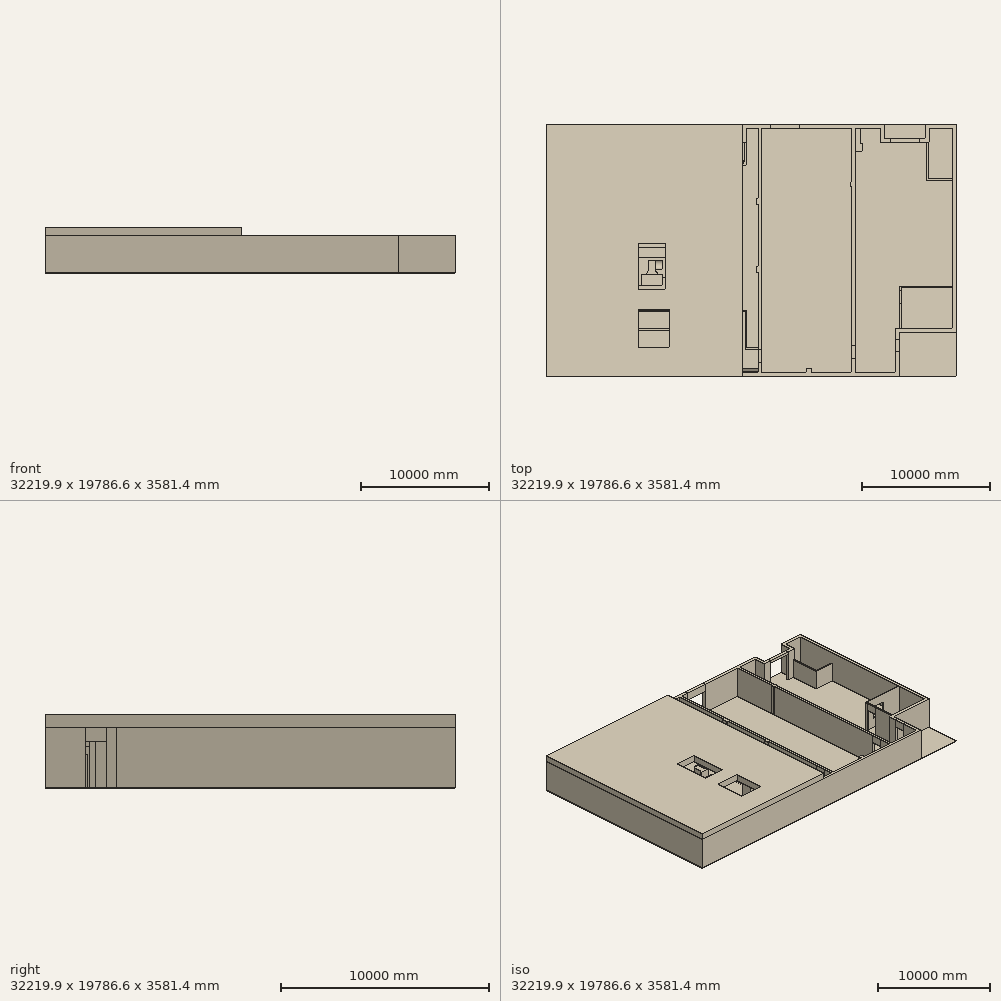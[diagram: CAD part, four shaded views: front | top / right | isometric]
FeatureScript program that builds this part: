
annotation { "Feature Type Name" : "Feature", "Feature Type Description" : "" }
export const myFeature = defineFeature(function(context is Context, id is Id, definition is map)
    precondition{}
    {
        {
            var Q0;
            Q0=qCreatedBy(makeId("Top.planeOp"),FACE);
            var sketch = newSketch(context, id + "F0", { "sketchPlane" : qUnion([Q0])});
            skLineSegment(sketch, "E0.bottom", {"start": v(-292.1, 292.1) * mm, "end": v(31927.8, 292.1) * mm});
            skLineSegment(sketch, "E0.top", {"start": v(-292.1, -19494.5) * mm, "end": v(31927.8, -19494.5) * mm});
            skLineSegment(sketch, "E0.left", {"start": v(-292.1, 292.1) * mm, "end": v(-292.1, -19494.5) * mm});
            skLineSegment(sketch, "E0.right", {"start": v(31927.8, 292.1) * mm, "end": v(31927.8, -19494.5) * mm});
            skSolve(sketch);
        }
        {
            var Q0;
            Q0 = qSketchRegion(id + "F0", true);
            extrude(context, id + "F1", {"entities" : qUnion([Q0]), "oppositeDirection" : true, "depth" : 50.8 * mm});
        }
        {
            var Q0;
            Q0=qCreatedBy(makeId("Top.planeOp"),FACE);
            var sketch = newSketch(context, id + "F2", { "sketchPlane" : qUnion([Q0])});
            skLineSegment(sketch, "E1.bottom", {"start": v(0, 0) * mm, "end": v(3479.8, 0) * mm});
            skLineSegment(sketch, "E1.top", {"start": v(0, -18897.6) * mm, "end": v(6451.6, -18897.6) * mm, "construction": true});
            skLineSegment(sketch, "E1.left", {"start": v(0, 0) * mm, "end": v(0, -18897.6) * mm});
            skLineSegment(sketch, "E1.right", {"start": v(16332.2, 0) * mm, "end": v(16332.2, -5537.2) * mm});
            skLineSegment(sketch, "E2.top", {"start": v(0, -19202.4) * mm, "end": v(6451.6, -19202.4) * mm});
            skLineSegment(sketch, "E2.left", {"start": v(0, -18897.6) * mm, "end": v(0, -19202.4) * mm});
            skLineSegment(sketch, "E2.right", {"start": v(16332.2, -18897.6) * mm, "end": v(16332.2, -19202.4) * mm});
            skLineSegment(sketch, "E3", {"start": v(0, -4508.5) * mm, "end": v(3479.8, -4508.5) * mm, "construction": true});
            skLineSegment(sketch, "E4", {"start": v(3479.8, -4508.5) * mm, "end": v(3479.8, -4457.7) * mm, "construction": true});
            skLineSegment(sketch, "E5", {"start": v(3479.8, -4457.7) * mm, "end": v(3594.1, -4457.7) * mm, "construction": true});
            skLineSegment(sketch, "E6", {"start": v(3594.1, -4457.7) * mm, "end": v(3594.1, -4622.8) * mm, "construction": true});
            skLineSegment(sketch, "E7", {"start": v(3594.1, -4622.8) * mm, "end": v(0, -4622.8) * mm, "construction": true});
            skLineSegment(sketch, "E8", {"start": v(3479.8, 0) * mm, "end": v(3479.8, -1117.6) * mm});
            skLineSegment(sketch, "E9", {"start": v(3479.8, -1117.6) * mm, "end": v(4267.2, -1117.6) * mm});
            skLineSegment(sketch, "E10", {"start": v(4267.2, -1117.6) * mm, "end": v(4267.2, -825.5) * mm});
            skLineSegment(sketch, "E11", {"start": v(4267.2, -825.5) * mm, "end": v(3771.9, -825.5) * mm});
            skLineSegment(sketch, "E12", {"start": v(3771.9, -825.5) * mm, "end": v(3771.9, 0) * mm});
            skLineSegment(sketch, "E13", {"start": v(5295.9, -825.5) * mm, "end": v(5295.9, -1117.6) * mm});
            skLineSegment(sketch, "E14", {"start": v(5295.9, -1117.6) * mm, "end": v(6096, -1117.6) * mm});
            skLineSegment(sketch, "E15", {"start": v(6096, -1117.6) * mm, "end": v(6096, 0) * mm});
            skLineSegment(sketch, "E16", {"start": v(5295.9, -825.5) * mm, "end": v(5803.9, -825.5) * mm});
            skLineSegment(sketch, "E17", {"start": v(5803.9, -825.5) * mm, "end": v(5803.9, 0) * mm});
            skLineSegment(sketch, "E18", {"start": v(3479.8, -1117.6) * mm, "end": v(3479.8, -3543.3) * mm, "construction": true});
            skLineSegment(sketch, "E19", {"start": v(3479.8, -3543.3) * mm, "end": v(3594.1, -3543.3) * mm, "construction": true});
            skLineSegment(sketch, "E20", {"start": v(3594.1, -3543.3) * mm, "end": v(3594.1, -1117.6) * mm, "construction": true});
            skLineSegment(sketch, "E21", {"start": v(11582.4, 0) * mm, "end": v(11582.4, -1117.6) * mm});
            skLineSegment(sketch, "E22", {"start": v(11582.4, -1117.6) * mm, "end": v(12382.5, -1117.6) * mm});
            skLineSegment(sketch, "E23", {"start": v(12382.5, -1117.6) * mm, "end": v(12382.5, -825.5) * mm});
            skLineSegment(sketch, "E24", {"start": v(12382.5, -825.5) * mm, "end": v(11874.5, -825.5) * mm});
            skLineSegment(sketch, "E25", {"start": v(11874.5, -825.5) * mm, "end": v(11874.5, 0) * mm});
            skLineSegment(sketch, "E26", {"start": v(15113, 0) * mm, "end": v(15113, -825.5) * mm});
            skLineSegment(sketch, "E27", {"start": v(15113, -825.5) * mm, "end": v(14605, -825.5) * mm});
            skLineSegment(sketch, "E28", {"start": v(14605, -825.5) * mm, "end": v(14605, -1117.6) * mm});
            skLineSegment(sketch, "E29", {"start": v(14605, -1117.6) * mm, "end": v(15405.1, -1117.6) * mm});
            skLineSegment(sketch, "E30", {"start": v(15405.1, -1117.6) * mm, "end": v(15405.1, 0) * mm});
            skLineSegment(sketch, "E31", {"start": v(3771.9, 0) * mm, "end": v(3771.9, 292.1) * mm});
            skLineSegment(sketch, "E32", {"start": v(3771.9, 292.1) * mm, "end": v(-292.1, 292.1) * mm});
            skLineSegment(sketch, "E33", {"start": v(-292.1, 292.1) * mm, "end": v(-292.1, -19494.5) * mm});
            skLineSegment(sketch, "E34", {"start": v(-292.1, -19494.5) * mm, "end": v(16624.3, -19494.5) * mm});
            skLineSegment(sketch, "E35", {"start": v(16624.3, -19202.4) * mm, "end": v(16624.3, -18376.9) * mm});
            skLineSegment(sketch, "E36", {"start": v(16624.3, 292.1) * mm, "end": v(15113, 292.1) * mm});
            skLineSegment(sketch, "E37", {"start": v(15113, 292.1) * mm, "end": v(15113, 0) * mm});
            skLineSegment(sketch, "E38", {"start": v(5803.9, 0) * mm, "end": v(5803.9, 292.1) * mm});
            skLineSegment(sketch, "E39", {"start": v(5803.9, 292.1) * mm, "end": v(11874.5, 292.1) * mm});
            skLineSegment(sketch, "E40", {"start": v(11874.5, 292.1) * mm, "end": v(11874.5, 0) * mm});
            skLineSegment(sketch, "E41.trimOffspring", {"start": v(6096, 0) * mm, "end": v(11582.4, 0) * mm});
            skLineSegment(sketch, "E42.trimOffspring", {"start": v(15405.1, 0) * mm, "end": v(16332.2, 0) * mm});
            skLineSegment(sketch, "E43", {"start": v(16332.2, -18376.9) * mm, "end": v(16624.3, -18376.9) * mm});
            skLineSegment(sketch, "E44", {"start": v(16624.3, -17348.2) * mm, "end": v(16332.2, -17348.2) * mm});
            skLineSegment(sketch, "E45.trimOffspring", {"start": v(16332.2, -18376.9) * mm, "end": v(16332.2, -18897.6) * mm});
            skLineSegment(sketch, "E46.trimOffspring", {"start": v(16624.3, -17348.2) * mm, "end": v(16624.3, 0) * mm});
            skLineSegment(sketch, "E47", {"start": v(16332.2, -5537.2) * mm, "end": v(16230.6, -5537.2) * mm});
            skLineSegment(sketch, "E48", {"start": v(16230.6, -5537.2) * mm, "end": v(16230.6, -6007.1) * mm});
            skLineSegment(sketch, "E49", {"start": v(16230.6, -6007.1) * mm, "end": v(16332.2, -6007.1) * mm});
            skLineSegment(sketch, "E50", {"start": v(16332.2, -10833.1) * mm, "end": v(16230.6, -10833.1) * mm});
            skLineSegment(sketch, "E51", {"start": v(16230.6, -10833.1) * mm, "end": v(16230.6, -11303) * mm});
            skLineSegment(sketch, "E52", {"start": v(16230.6, -11303) * mm, "end": v(16332.2, -11303) * mm});
            skLineSegment(sketch, "E53.trimOffspring", {"start": v(16332.2, -11303) * mm, "end": v(16332.2, -17348.2) * mm});
            skLineSegment(sketch, "E54.trimOffspring", {"start": v(16332.2, -6007.1) * mm, "end": v(16332.2, -10833.1) * mm});
            skLineSegment(sketch, "E55", {"start": v(6451.6, -19202.4) * mm, "end": v(6451.6, -18897.6) * mm});
            skLineSegment(sketch, "E56", {"start": v(6845.3, -19202.4) * mm, "end": v(6845.3, -18897.6) * mm});
            skLineSegment(sketch, "E57", {"start": v(9982.2, -19151.6) * mm, "end": v(9982.2, -18897.6) * mm});
            skLineSegment(sketch, "E58", {"start": v(10337.8, -19151.6) * mm, "end": v(10337.8, -18897.6) * mm});
            skLineSegment(sketch, "E59", {"start": v(13309.6, -19202.4) * mm, "end": v(13309.6, -18897.6) * mm});
            skLineSegment(sketch, "E60", {"start": v(13700.76, -19202.4) * mm, "end": v(13700.76, -18897.6) * mm});
            skLineSegment(sketch, "E61.trimOffspring", {"start": v(6845.3, -18897.6) * mm, "end": v(9982.2, -18897.6) * mm, "construction": true});
            skLineSegment(sketch, "E62.trimOffspring", {"start": v(6845.3, -19202.4) * mm, "end": v(9982.2, -19202.4) * mm});
            skLineSegment(sketch, "E63.trimOffspring", {"start": v(10337.8, -18897.6) * mm, "end": v(13309.6, -18897.6) * mm, "construction": true});
            skLineSegment(sketch, "E64.trimOffspring", {"start": v(10337.8, -19202.4) * mm, "end": v(13309.6, -19202.4) * mm});
            skLineSegment(sketch, "E65.trimOffspring", {"start": v(13700.76, -18897.6) * mm, "end": v(16332.2, -18897.6) * mm, "construction": true});
            skLineSegment(sketch, "E66.trimOffspring", {"start": v(13700.76, -19202.4) * mm, "end": v(16332.2, -19202.4) * mm});
            skLineSegment(sketch, "E67", {"start": v(6451.6, -18897.6) * mm, "end": v(6845.3, -18897.6) * mm});
            skLineSegment(sketch, "E68", {"start": v(9982.2, -18897.6) * mm, "end": v(10337.8, -18897.6) * mm});
            skLineSegment(sketch, "E69", {"start": v(13309.6, -18897.6) * mm, "end": v(13700.76, -18897.6) * mm});
            skLineSegment(sketch, "E70", {"start": v(9982.2, -19151.6) * mm, "end": v(10337.8, -19151.6) * mm});
            skLineSegment(sketch, "E71", {"start": v(10337.8, -19202.4) * mm, "end": v(9982.2, -19202.4) * mm});
            skLineSegment(sketch, "E72.bottom", {"start": v(9944.1, -4292.6) * mm, "end": v(10261.6, -4292.6) * mm});
            skLineSegment(sketch, "E72.top", {"start": v(9944.1, -4610.1) * mm, "end": v(10261.6, -4610.1) * mm});
            skLineSegment(sketch, "E72.left", {"start": v(9944.1, -4292.6) * mm, "end": v(9944.1, -4610.1) * mm});
            skLineSegment(sketch, "E72.right", {"start": v(10261.6, -4292.6) * mm, "end": v(10261.6, -4610.1) * mm});
            skLineSegment(sketch, "E73", {"start": v(16332.2, -18897.6) * mm, "end": v(34945.72, -18897.6) * mm, "construction": true});
            skLineSegment(sketch, "E74", {"start": v(16624.3, -19202.4) * mm, "end": v(20129.5, -19202.4) * mm});
            skLineSegment(sketch, "E75", {"start": v(16624.3, -19494.5) * mm, "end": v(27432, -19494.5) * mm});
            skLineSegment(sketch, "E76", {"start": v(27432, -19494.5) * mm, "end": v(27432, -17576.8) * mm});
            skLineSegment(sketch, "E77", {"start": v(27432, -16052.8) * mm, "end": v(31927.8, -16052.8) * mm});
            skLineSegment(sketch, "E78", {"start": v(31927.8, -16052.8) * mm, "end": v(31927.8, 292.1) * mm});
            skLineSegment(sketch, "E79", {"start": v(16624.3, 0) * mm, "end": v(17335.5, 0) * mm});
            skLineSegment(sketch, "E80", {"start": v(25946.1, 0) * mm, "end": v(25946.1, -1117.6) * mm});
            skLineSegment(sketch, "E81", {"start": v(25946.1, -1117.6) * mm, "end": v(26746.2, -1117.6) * mm});
            skLineSegment(sketch, "E82", {"start": v(26746.2, -1117.6) * mm, "end": v(26746.2, -825.5) * mm});
            skLineSegment(sketch, "E83", {"start": v(26746.2, -825.5) * mm, "end": v(26238.2, -825.5) * mm});
            skLineSegment(sketch, "E84", {"start": v(26238.2, -825.5) * mm, "end": v(26238.2, 292.1) * mm});
            skLineSegment(sketch, "E85", {"start": v(26238.2, 292.1) * mm, "end": v(19558, 292.1) * mm});
            skLineSegment(sketch, "E86", {"start": v(17335.5, 292.1) * mm, "end": v(17335.5, 0) * mm});
            skLineSegment(sketch, "E87", {"start": v(19558, 0) * mm, "end": v(19558, 292.1) * mm});
            skLineSegment(sketch, "E88.trimOffspring", {"start": v(17335.5, 292.1) * mm, "end": v(16624.3, 292.1) * mm});
            skLineSegment(sketch, "E89.trimOffspring", {"start": v(19558, 0) * mm, "end": v(23672.8, 0) * mm});
            skLineSegment(sketch, "E90", {"start": v(23672.8, 0) * mm, "end": v(23672.8, -4292.6) * mm});
            skLineSegment(sketch, "E91", {"start": v(23964.9, 0) * mm, "end": v(23964.9, -4292.6) * mm});
            skLineSegment(sketch, "E92", {"start": v(23964.9, -19202.4) * mm, "end": v(27139.9, -19202.4) * mm});
            skLineSegment(sketch, "E93", {"start": v(27139.9, -19202.4) * mm, "end": v(27139.9, -17576.8) * mm});
            skLineSegment(sketch, "E94", {"start": v(27139.9, -15760.7) * mm, "end": v(31635.7, -15760.7) * mm});
            skLineSegment(sketch, "E95", {"start": v(31635.7, -15760.7) * mm, "end": v(31635.7, 0) * mm});
            skLineSegment(sketch, "E96", {"start": v(31635.7, 0) * mm, "end": v(29781.5, 0) * mm});
            skLineSegment(sketch, "E97", {"start": v(29781.5, 0) * mm, "end": v(29781.5, -1117.6) * mm});
            skLineSegment(sketch, "E98", {"start": v(29781.5, -1117.6) * mm, "end": v(28981.4, -1117.6) * mm});
            skLineSegment(sketch, "E99", {"start": v(28981.4, -1117.6) * mm, "end": v(28981.4, -825.5) * mm});
            skLineSegment(sketch, "E100", {"start": v(28981.4, -825.5) * mm, "end": v(29489.4, -825.5) * mm});
            skLineSegment(sketch, "E101", {"start": v(29489.4, -825.5) * mm, "end": v(29489.4, 292.1) * mm});
            skLineSegment(sketch, "E102", {"start": v(29489.4, 292.1) * mm, "end": v(31927.8, 292.1) * mm});
            skLineSegment(sketch, "E103.trimOffspring", {"start": v(23964.9, 0) * mm, "end": v(25946.1, 0) * mm});
            skLineSegment(sketch, "E104", {"start": v(27139.9, -16560.8) * mm, "end": v(27432, -16560.8) * mm});
            skLineSegment(sketch, "E105", {"start": v(27139.9, -17576.8) * mm, "end": v(27432, -17576.8) * mm});
            skLineSegment(sketch, "E106.trimOffspring", {"start": v(27432, -16560.8) * mm, "end": v(27432, -16052.8) * mm});
            skLineSegment(sketch, "E107.trimOffspring", {"start": v(27139.9, -16560.8) * mm, "end": v(27139.9, -15760.7) * mm});
            skLineSegment(sketch, "E108", {"start": v(20129.5, -19202.4) * mm, "end": v(20129.5, -18897.6) * mm});
            skLineSegment(sketch, "E109", {"start": v(20129.5, -18897.6) * mm, "end": v(20535.9, -18897.6) * mm});
            skLineSegment(sketch, "E110", {"start": v(20535.9, -18897.6) * mm, "end": v(20535.9, -19202.4) * mm});
            skLineSegment(sketch, "E111.trimOffspring", {"start": v(20535.9, -19202.4) * mm, "end": v(23672.8, -19202.4) * mm});
            skLineSegment(sketch, "E112", {"start": v(23672.8, -17068.8) * mm, "end": v(23964.9, -17068.8) * mm});
            skLineSegment(sketch, "E113", {"start": v(23964.9, -18084.8) * mm, "end": v(23672.8, -18084.8) * mm});
            skLineSegment(sketch, "E114.trimOffspring", {"start": v(23964.9, -18084.8) * mm, "end": v(23964.9, -19202.4) * mm});
            skLineSegment(sketch, "E115.trimOffspring", {"start": v(23672.8, -18084.8) * mm, "end": v(23672.8, -19202.4) * mm});
            skLineSegment(sketch, "E116", {"start": v(23672.8, -4292.6) * mm, "end": v(23634.7, -4292.6) * mm});
            skLineSegment(sketch, "E117", {"start": v(23634.7, -4292.6) * mm, "end": v(23634.7, -4610.1) * mm});
            skLineSegment(sketch, "E118", {"start": v(23634.7, -4610.1) * mm, "end": v(23672.8, -4610.1) * mm});
            skLineSegment(sketch, "E119", {"start": v(23964.9, -4292.6) * mm, "end": v(24003, -4292.6) * mm});
            skLineSegment(sketch, "E120", {"start": v(24003, -4292.6) * mm, "end": v(24003, -4610.1) * mm});
            skLineSegment(sketch, "E121", {"start": v(24003, -4610.1) * mm, "end": v(23964.9, -4610.1) * mm});
            skLineSegment(sketch, "E122.trimOffspring", {"start": v(23672.8, -4610.1) * mm, "end": v(23672.8, -17068.8) * mm});
            skLineSegment(sketch, "E123.trimOffspring", {"start": v(23964.9, -4610.1) * mm, "end": v(23964.9, -17068.8) * mm});
            skSolve(sketch);
        }
        {
            var Q0;
            Q0 = qSketchRegion(id + "F2", true);
            extrude(context, id + "F3", {"entities" : qUnion([Q0]), "depth" : 2921 * mm});
        }
        {
            var Q0;
            Q0=makeQuery(id+"F3.opExtrude","SWEPT_FACE",FACE,{"disambiguationData":[OSD([sQuery(id+"F2.wireOp",EDGE,"E2.right"),sQuery(id+"F2.wireOp",EDGE,"E45.trimOffspring")])]});
            var sketch = newSketch(context, id + "F4", { "sketchPlane" : qUnion([Q0])});
            skLineSegment(sketch, "E124", {"start": v(19202.4, 0) * mm, "end": v(18897.6, 0) * mm});
            skLineSegment(sketch, "E125", {"start": v(18897.6, 0) * mm, "end": v(18897.6, 203.2) * mm});
            skLineSegment(sketch, "E126", {"start": v(18897.6, 203.2) * mm, "end": v(19100.8, 457.2) * mm});
            skLineSegment(sketch, "E127", {"start": v(19202.4, 457.2) * mm, "end": v(19202.4, 0) * mm});
            skLineSegment(sketch, "E128", {"start": v(19202.4, 457.2) * mm, "end": v(19100.8, 457.2) * mm});
            skSolve(sketch);
        }
        {
            var Q0;
            Q0 = qSketchRegion(id + "F4", true);
            var Q1;
            Q1=makeQuery(id+"F3.opExtrude","SWEPT_FACE",FACE,{"disambiguationData":[OSD([sQuery(id+"F2.wireOp",EDGE,"E1.left"),sQuery(id+"F2.wireOp",EDGE,"E2.left")])]});
            extrude(context, id + "F5", {"entities" : qUnion([Q0]), "endBound" : BoundingType.UP_TO_SURFACE, "endBoundEntityFace" : qUnion([Q1]), "depth" : 25.4 * mm});
        }
        {
            var Q0;
            Q0=makeQuery(id+"F1.opExtrude","CAP_FACE",FACE,{"disambiguationData":[OSD([sQuery(id+"F0.wireOp",EDGE,"E0.bottom"),sQuery(id+"F0.wireOp",EDGE,"E0.top"),sQuery(id+"F0.wireOp",EDGE,"E0.left"),sQuery(id+"F0.wireOp",EDGE,"E0.right")])],"isStart":true});
            var sketch = newSketch(context, id + "F6", { "sketchPlane" : qUnion([Q0])});
            skLineSegment(sketch, "E129", {"start": v(3479.8, -1117.6) * mm, "end": v(3479.8, -3543.3) * mm});
            skLineSegment(sketch, "E130", {"start": v(3479.8, -3543.3) * mm, "end": v(3594.1, -3543.3) * mm});
            skLineSegment(sketch, "E131", {"start": v(3594.1, -3543.3) * mm, "end": v(3594.1, -1117.6) * mm});
            skLineSegment(sketch, "E132", {"start": v(3594.1, -1117.6) * mm, "end": v(3479.8, -1117.6) * mm});
            skLineSegment(sketch, "E133", {"start": v(0, -4508.5) * mm, "end": v(3479.8, -4508.5) * mm});
            skLineSegment(sketch, "E134", {"start": v(3479.8, -4508.5) * mm, "end": v(3479.8, -4457.7) * mm});
            skLineSegment(sketch, "E135", {"start": v(3479.8, -4457.7) * mm, "end": v(3594.1, -4457.7) * mm});
            skLineSegment(sketch, "E136", {"start": v(3594.1, -4457.7) * mm, "end": v(3594.1, -4622.8) * mm});
            skLineSegment(sketch, "E137", {"start": v(3594.1, -4622.8) * mm, "end": v(0, -4622.8) * mm});
            skLineSegment(sketch, "E138", {"start": v(0, -4622.8) * mm, "end": v(0, -4508.5) * mm});
            skSolve(sketch);
        }
        {
            var Q0;
            Q0 = qSketchRegion(id + "F6", true);
            extrude(context, id + "F7", {"entities" : qUnion([Q0]), "depth" : 2921 * mm});
        }
        {
            var Q0;
            Q0=makeQuery(id+"F3.opExtrude","CAP_FACE",FACE,{"disambiguationData":[OSD([sQuery(id+"F2.wireOp",EDGE,"E13"),sQuery(id+"F2.wireOp",EDGE,"E14"),sQuery(id+"F2.wireOp",EDGE,"E15"),sQuery(id+"F2.wireOp",EDGE,"E16"),sQuery(id+"F2.wireOp",EDGE,"E17"),sQuery(id+"F2.wireOp",EDGE,"E21"),sQuery(id+"F2.wireOp",EDGE,"E22"),sQuery(id+"F2.wireOp",EDGE,"E23"),sQuery(id+"F2.wireOp",EDGE,"E24"),sQuery(id+"F2.wireOp",EDGE,"E25"),sQuery(id+"F2.wireOp",EDGE,"E38"),sQuery(id+"F2.wireOp",EDGE,"E39"),sQuery(id+"F2.wireOp",EDGE,"E40"),sQuery(id+"F2.wireOp",EDGE,"E41.trimOffspring")])],"isStart":false});
            var sketch = newSketch(context, id + "F8", { "sketchPlane" : qUnion([Q0])});
            skLineSegment(sketch, "E139.bottom", {"start": v(4267.2, -825.5) * mm, "end": v(5295.9, -825.5) * mm});
            skLineSegment(sketch, "E139.top", {"start": v(4267.2, -1117.6) * mm, "end": v(5295.9, -1117.6) * mm});
            skLineSegment(sketch, "E139.left", {"start": v(4267.2, -825.5) * mm, "end": v(4267.2, -1117.6) * mm});
            skLineSegment(sketch, "E139.right", {"start": v(5295.9, -825.5) * mm, "end": v(5295.9, -1117.6) * mm});
            skLineSegment(sketch, "E140.bottom", {"start": v(16624.3, -17348.2) * mm, "end": v(16332.2, -17348.2) * mm});
            skLineSegment(sketch, "E140.top", {"start": v(16624.3, -18376.9) * mm, "end": v(16332.2, -18376.9) * mm});
            skLineSegment(sketch, "E140.left", {"start": v(16624.3, -17348.2) * mm, "end": v(16624.3, -18376.9) * mm});
            skLineSegment(sketch, "E140.right", {"start": v(16332.2, -17348.2) * mm, "end": v(16332.2, -18376.9) * mm});
            skLineSegment(sketch, "E141.bottom", {"start": v(23672.8, -17068.8) * mm, "end": v(23964.9, -17068.8) * mm});
            skLineSegment(sketch, "E141.top", {"start": v(23672.8, -18084.8) * mm, "end": v(23964.9, -18084.8) * mm});
            skLineSegment(sketch, "E141.left", {"start": v(23672.8, -17068.8) * mm, "end": v(23672.8, -18084.8) * mm});
            skLineSegment(sketch, "E141.right", {"start": v(23964.9, -17068.8) * mm, "end": v(23964.9, -18084.8) * mm});
            skLineSegment(sketch, "E142.bottom", {"start": v(27139.9, -16560.8) * mm, "end": v(27432, -16560.8) * mm});
            skLineSegment(sketch, "E142.top", {"start": v(27139.9, -17576.8) * mm, "end": v(27432, -17576.8) * mm});
            skLineSegment(sketch, "E142.left", {"start": v(27139.9, -16560.8) * mm, "end": v(27139.9, -17576.8) * mm});
            skLineSegment(sketch, "E142.right", {"start": v(27432, -16560.8) * mm, "end": v(27432, -17576.8) * mm});
            skLineSegment(sketch, "E143.bottom", {"start": v(17335.5, 292.1) * mm, "end": v(19558, 292.1) * mm});
            skLineSegment(sketch, "E143.top", {"start": v(17335.5, 0) * mm, "end": v(19558, 0) * mm});
            skLineSegment(sketch, "E143.left", {"start": v(17335.5, 292.1) * mm, "end": v(17335.5, 0) * mm});
            skLineSegment(sketch, "E143.right", {"start": v(19558, 292.1) * mm, "end": v(19558, 0) * mm});
            skSolve(sketch);
        }
        {
            var Q0;
            Q0 = qSketchRegion(id + "F8", true);
            extrude(context, id + "F9", {"entities" : qUnion([Q0]), "oppositeDirection" : true, "depth" : 711.2 * mm});
        }
        {
            var Q0;
            Q0=makeQuery(id+"F3.opExtrude","CAP_FACE",FACE,{"disambiguationData":[OSD([sQuery(id+"F2.wireOp",EDGE,"E1.right"),sQuery(id+"F2.wireOp",EDGE,"E26"),sQuery(id+"F2.wireOp",EDGE,"E27"),sQuery(id+"F2.wireOp",EDGE,"E28"),sQuery(id+"F2.wireOp",EDGE,"E29"),sQuery(id+"F2.wireOp",EDGE,"E30"),sQuery(id+"F2.wireOp",EDGE,"E36"),sQuery(id+"F2.wireOp",EDGE,"E37"),sQuery(id+"F2.wireOp",EDGE,"E42.trimOffspring"),sQuery(id+"F2.wireOp",EDGE,"E44"),sQuery(id+"F2.wireOp",EDGE,"E46.trimOffspring"),sQuery(id+"F2.wireOp",EDGE,"E47"),sQuery(id+"F2.wireOp",EDGE,"E48"),sQuery(id+"F2.wireOp",EDGE,"E49"),sQuery(id+"F2.wireOp",EDGE,"E50"),sQuery(id+"F2.wireOp",EDGE,"E51"),sQuery(id+"F2.wireOp",EDGE,"E52"),sQuery(id+"F2.wireOp",EDGE,"E53.trimOffspring"),sQuery(id+"F2.wireOp",EDGE,"E54.trimOffspring")])],"isStart":false});
            var sketch = newSketch(context, id + "F10", { "sketchPlane" : qUnion([Q0])});
            skLineSegment(sketch, "E144.bottom", {"start": v(12382.5, -825.5) * mm, "end": v(14605, -825.5) * mm});
            skLineSegment(sketch, "E144.top", {"start": v(12382.5, -1117.6) * mm, "end": v(14605, -1117.6) * mm});
            skLineSegment(sketch, "E144.left", {"start": v(12382.5, -825.5) * mm, "end": v(12382.5, -1117.6) * mm});
            skLineSegment(sketch, "E144.right", {"start": v(14605, -825.5) * mm, "end": v(14605, -1117.6) * mm});
            skLineSegment(sketch, "E145.bottom", {"start": v(26746.2, -825.5) * mm, "end": v(28981.4, -825.5) * mm});
            skLineSegment(sketch, "E145.top", {"start": v(26746.2, -1117.6) * mm, "end": v(28981.4, -1117.6) * mm});
            skLineSegment(sketch, "E145.left", {"start": v(26746.2, -825.5) * mm, "end": v(26746.2, -1117.6) * mm});
            skLineSegment(sketch, "E145.right", {"start": v(28981.4, -825.5) * mm, "end": v(28981.4, -1117.6) * mm});
            skSolve(sketch);
        }
        {
            var Q0;
            Q0 = qSketchRegion(id + "F10", true);
            extrude(context, id + "F11", {"entities" : qUnion([Q0]), "oppositeDirection" : true, "depth" : 304.8 * mm});
        }
        {
            var Q0;
            Q0=makeQuery(id+"F1.opExtrude","CAP_FACE",FACE,{"disambiguationData":[OSD([sQuery(id+"F0.wireOp",EDGE,"E0.bottom"),sQuery(id+"F0.wireOp",EDGE,"E0.top"),sQuery(id+"F0.wireOp",EDGE,"E0.left"),sQuery(id+"F0.wireOp",EDGE,"E0.right")])],"isStart":true});
            var sketch = newSketch(context, id + "F12", { "sketchPlane" : qUnion([Q0])});
            skLineSegment(sketch, "E146", {"start": v(6096, -1117.6) * mm, "end": v(6096, -4622.8) * mm});
            skLineSegment(sketch, "E147", {"start": v(6096, -4622.8) * mm, "end": v(5486.4, -4622.8) * mm});
            skLineSegment(sketch, "E148", {"start": v(3594.1, -4622.8) * mm, "end": v(3594.1, -4514.85) * mm});
            skLineSegment(sketch, "E149", {"start": v(3594.1, -4514.85) * mm, "end": v(5884.22, -4514.85) * mm});
            skLineSegment(sketch, "E150", {"start": v(5988.05, -4451.67) * mm, "end": v(5988.05, -3202.86) * mm});
            skLineSegment(sketch, "E151", {"start": v(5988.05, -1117.6) * mm, "end": v(6096, -1117.6) * mm});
            skLineSegment(sketch, "E152", {"start": v(3962.4, -4622.8) * mm, "end": v(3962.4, -15849.6) * mm});
            skLineSegment(sketch, "E153", {"start": v(3962.4, -15849.6) * mm, "end": v(13893.8, -15849.6) * mm});
            skLineSegment(sketch, "E154", {"start": v(13893.8, -15849.6) * mm, "end": v(13893.8, -18897.6) * mm});
            skLineSegment(sketch, "E155", {"start": v(13893.8, -18897.6) * mm, "end": v(14001.75, -18897.6) * mm});
            skLineSegment(sketch, "E156", {"start": v(14001.75, -18897.6) * mm, "end": v(14001.75, -15741.65) * mm});
            skLineSegment(sketch, "E157", {"start": v(14001.75, -15741.65) * mm, "end": v(4070.35, -15741.65) * mm});
            skLineSegment(sketch, "E158", {"start": v(4070.35, -15741.65) * mm, "end": v(4070.35, -4622.8) * mm});
            skLineSegment(sketch, "E159", {"start": v(5378.45, -4622.8) * mm, "end": v(5378.45, -14433.55) * mm});
            skLineSegment(sketch, "E160", {"start": v(5378.45, -14433.55) * mm, "end": v(12839.7, -14433.55) * mm});
            skLineSegment(sketch, "E161", {"start": v(12731.75, -14325.6) * mm, "end": v(5486.4, -14325.6) * mm});
            skLineSegment(sketch, "E162", {"start": v(5486.4, -14325.6) * mm, "end": v(5486.4, -4622.8) * mm});
            skLineSegment(sketch, "E163.trimOffspring", {"start": v(3962.4, -4622.8) * mm, "end": v(3594.1, -4622.8) * mm});
            skLineSegment(sketch, "E164.trimOffspring", {"start": v(5378.45, -4622.8) * mm, "end": v(4070.35, -4622.8) * mm});
            skLineSegment(sketch, "E165", {"start": v(11582.4, -1117.6) * mm, "end": v(11582.4, -2946.4) * mm});
            skLineSegment(sketch, "E166", {"start": v(11582.4, -2946.4) * mm, "end": v(12731.75, -2946.4) * mm});
            skLineSegment(sketch, "E167", {"start": v(12731.75, -2946.4) * mm, "end": v(12731.75, -14325.6) * mm});
            skLineSegment(sketch, "E168", {"start": v(12839.7, -14433.55) * mm, "end": v(12839.7, -2946.4) * mm});
            skLineSegment(sketch, "E169", {"start": v(12839.7, -2946.4) * mm, "end": v(14147.8, -2946.4) * mm});
            skLineSegment(sketch, "E170", {"start": v(14147.8, -2946.4) * mm, "end": v(14147.8, -14433.55) * mm});
            skLineSegment(sketch, "E171", {"start": v(14147.8, -14433.55) * mm, "end": v(15309.85, -14433.55) * mm});
            skLineSegment(sketch, "E172", {"start": v(15309.85, -14433.55) * mm, "end": v(15309.85, -17348.2) * mm});
            skLineSegment(sketch, "E173", {"start": v(15309.85, -17348.2) * mm, "end": v(16332.2, -17348.2) * mm});
            skLineSegment(sketch, "E174", {"start": v(16332.2, -17348.2) * mm, "end": v(16332.2, -17240.25) * mm});
            skLineSegment(sketch, "E175", {"start": v(16332.2, -17240.25) * mm, "end": v(15417.8, -17240.25) * mm});
            skLineSegment(sketch, "E176", {"start": v(15417.8, -17240.25) * mm, "end": v(15417.8, -14325.6) * mm});
            skLineSegment(sketch, "E177", {"start": v(15417.8, -14325.6) * mm, "end": v(14255.75, -14325.6) * mm});
            skLineSegment(sketch, "E178", {"start": v(14255.75, -14325.6) * mm, "end": v(14255.75, -2946.4) * mm});
            skLineSegment(sketch, "E179", {"start": v(14255.75, -2946.4) * mm, "end": v(15405.1, -2946.4) * mm});
            skLineSegment(sketch, "E180", {"start": v(15405.1, -2946.4) * mm, "end": v(15405.1, -1117.6) * mm});
            skLineSegment(sketch, "E181", {"start": v(15405.1, -1117.6) * mm, "end": v(15297.15, -1117.6) * mm});
            skLineSegment(sketch, "E182", {"start": v(15297.15, -1117.6) * mm, "end": v(15297.15, -2750.9) * mm});
            skLineSegment(sketch, "E183", {"start": v(15228.6, -2838.45) * mm, "end": v(14002.7, -2838.45) * mm});
            skLineSegment(sketch, "E184", {"start": v(11690.35, -2838.45) * mm, "end": v(11690.35, -1801.17) * mm});
            skLineSegment(sketch, "E185", {"start": v(11690.35, -1117.6) * mm, "end": v(11582.4, -1117.6) * mm});
            skLineSegment(sketch, "E186", {"start": v(5884.22, -4514.85) * mm, "end": v(3797.3, -3244.85) * mm});
            skLineSegment(sketch, "E187", {"start": v(3797.3, -3244.85) * mm, "end": v(3853.42, -3152.63) * mm});
            skLineSegment(sketch, "E188", {"start": v(3853.42, -3152.63) * mm, "end": v(5988.05, -4451.67) * mm});
            skLineSegment(sketch, "E189", {"start": v(5988.05, -3202.86) * mm, "end": v(3797.3, -1869.67) * mm});
            skLineSegment(sketch, "E190", {"start": v(3797.3, -1869.67) * mm, "end": v(3853.42, -1777.46) * mm});
            skLineSegment(sketch, "E191", {"start": v(3853.42, -1777.46) * mm, "end": v(5988.05, -3076.49) * mm});
            skLineSegment(sketch, "E192", {"start": v(5988.05, -1954.05) * mm, "end": v(4847.03, -1259.68) * mm});
            skLineSegment(sketch, "E193", {"start": v(4847.03, -1259.68) * mm, "end": v(4903.15, -1167.46) * mm});
            skLineSegment(sketch, "E194", {"start": v(4903.15, -1167.46) * mm, "end": v(5988.05, -1827.68) * mm});
            skLineSegment(sketch, "E195", {"start": v(3825.36, -3198.74) * mm, "end": v(5988.05, -4514.85) * mm, "construction": true});
            skLineSegment(sketch, "E196.trimOffspring", {"start": v(5988.05, -1827.68) * mm, "end": v(5988.05, -1117.6) * mm});
            skLineSegment(sketch, "E197.trimOffspring", {"start": v(5988.05, -3076.49) * mm, "end": v(5988.05, -1954.05) * mm});
            skLineSegment(sketch, "E198", {"start": v(15297.15, -2750.9) * mm, "end": v(13966.1, -1051.05) * mm});
            skLineSegment(sketch, "E199", {"start": v(13966.1, -1051.05) * mm, "end": v(13881.1, -1117.6) * mm});
            skLineSegment(sketch, "E200", {"start": v(13881.1, -1117.6) * mm, "end": v(15228.6, -2838.45) * mm});
            skLineSegment(sketch, "E201", {"start": v(14002.7, -2838.45) * mm, "end": v(12603.09, -1051.05) * mm});
            skLineSegment(sketch, "E202", {"start": v(12603.09, -1051.05) * mm, "end": v(12518.1, -1117.6) * mm});
            skLineSegment(sketch, "E203", {"start": v(12518.1, -1117.6) * mm, "end": v(13865.59, -2838.45) * mm});
            skLineSegment(sketch, "E204", {"start": v(12502.58, -2838.45) * mm, "end": v(11690.35, -1801.17) * mm});
            skLineSegment(sketch, "E205", {"start": v(12639.69, -2838.45) * mm, "end": v(11690.35, -1626.08) * mm});
            skLineSegment(sketch, "E206", {"start": v(13923.6, -1084.32) * mm, "end": v(15297.15, -2838.45) * mm, "construction": true});
            skLineSegment(sketch, "E207", {"start": v(12382.5, -1117.6) * mm, "end": v(14605, -1117.6) * mm, "construction": true});
            skLineSegment(sketch, "E208.trimOffspring", {"start": v(11690.35, -1626.08) * mm, "end": v(11690.35, -1117.6) * mm});
            skLineSegment(sketch, "E209.trimOffspring", {"start": v(12502.58, -2838.45) * mm, "end": v(11690.35, -2838.45) * mm});
            skLineSegment(sketch, "E210.trimOffspring", {"start": v(13865.59, -2838.45) * mm, "end": v(12639.69, -2838.45) * mm});
            skSolve(sketch);
        }
        {
            var Q0;
            Q0 = qSketchRegion(id + "F12", true);
            extrude(context, id + "F13", {"entities" : qUnion([Q0]), "depth" : 0.13 * mm});
        }
        {
            var Q0;
            Q0=makeQuery(id+"F7.opExtrude","SWEPT_FACE",FACE,{"disambiguationData":[OSD([sQuery(id+"F6.wireOp",EDGE,"E137")])]});
            var sketch = newSketch(context, id + "F14", { "sketchPlane" : qUnion([Q0])});
            skLineSegment(sketch, "E211.bottom", {"start": v(304.8, 2159) * mm, "end": v(1524, 2159) * mm});
            skLineSegment(sketch, "E211.top", {"start": v(304.8, 939.8) * mm, "end": v(1524, 939.8) * mm});
            skLineSegment(sketch, "E211.left", {"start": v(304.8, 2159) * mm, "end": v(304.8, 939.8) * mm});
            skLineSegment(sketch, "E211.right", {"start": v(1524, 2159) * mm, "end": v(1524, 939.8) * mm});
            skSolve(sketch);
        }
        {
            var Q0;
            Q0 = qSketchRegion(id + "F14", true);
            extrude(context, id + "F15", {"entities" : qUnion([Q0]), "operationType" : NewBodyOperationType.REMOVE, "oppositeDirection" : true, "depth" : 152.4 * mm});
        }
        {
            var Q0;
            Q0=makeQuery(id+"F7.opExtrude","SWEPT_FACE",FACE,{"disambiguationData":[OSD([sQuery(id+"F6.wireOp",EDGE,"E131")])]});
            var sketch = newSketch(context, id + "F16", { "sketchPlane" : qUnion([Q0])});
            skLineSegment(sketch, "E212.bottom", {"start": v(-1168.4, 2159) * mm, "end": v(-2387.6, 2159) * mm});
            skLineSegment(sketch, "E212.top", {"start": v(-1168.4, 939.8) * mm, "end": v(-2387.6, 939.8) * mm});
            skLineSegment(sketch, "E212.left", {"start": v(-1168.4, 2159) * mm, "end": v(-1168.4, 939.8) * mm});
            skLineSegment(sketch, "E212.right", {"start": v(-2387.6, 2159) * mm, "end": v(-2387.6, 939.8) * mm});
            skSolve(sketch);
        }
        {
            var Q0;
            Q0 = qSketchRegion(id + "F16", true);
            extrude(context, id + "F17", {"entities" : qUnion([Q0]), "operationType" : NewBodyOperationType.REMOVE, "oppositeDirection" : true, "depth" : 152.4 * mm});
        }
        {
            var Q0;
            Q0=makeQuery(id+"F3.opExtrude","SWEPT_FACE",FACE,{"disambiguationData":[OSD([sQuery(id+"F2.wireOp",EDGE,"E1.bottom")])]});
            var sketch = newSketch(context, id + "F18", { "sketchPlane" : qUnion([Q0])});
            skLineSegment(sketch, "E213.bottom", {"start": v(1143, 2247.9) * mm, "end": v(2362.2, 2247.9) * mm});
            skLineSegment(sketch, "E213.top", {"start": v(1143, 1028.7) * mm, "end": v(2362.2, 1028.7) * mm});
            skLineSegment(sketch, "E213.left", {"start": v(1143, 2247.9) * mm, "end": v(1143, 1028.7) * mm});
            skLineSegment(sketch, "E213.right", {"start": v(2362.2, 2247.9) * mm, "end": v(2362.2, 1028.7) * mm});
            skSolve(sketch);
        }
        {
            var Q0;
            Q0 = qSketchRegion(id + "F18", true);
            extrude(context, id + "F19", {"entities" : qUnion([Q0]), "operationType" : NewBodyOperationType.REMOVE, "oppositeDirection" : true, "depth" : 304.8 * mm});
        }
        {
            var Q0;
            Q0=makeQuery(id+"F3.opExtrude","SWEPT_FACE",FACE,{"disambiguationData":[OSD([sQuery(id+"F2.wireOp",EDGE,"E1.left"),sQuery(id+"F2.wireOp",EDGE,"E2.left")])]});
            var sketch = newSketch(context, id + "F20", { "sketchPlane" : qUnion([Q0])});
            skLineSegment(sketch, "E214.bottom", {"start": v(-10464.8, 0) * mm, "end": v(-13309.6, 0) * mm});
            skLineSegment(sketch, "E214.top", {"start": v(-10464.8, 2921) * mm, "end": v(-13309.6, 2921) * mm});
            skLineSegment(sketch, "E214.left", {"start": v(-10464.8, 0) * mm, "end": v(-10464.8, 2921) * mm});
            skLineSegment(sketch, "E214.right", {"start": v(-13309.6, 0) * mm, "end": v(-13309.6, 2921) * mm});
            skSolve(sketch);
        }
        {
            var Q0;
            Q0 = qSketchRegion(id + "F20", true);
            extrude(context, id + "F21", {"entities" : qUnion([Q0]), "depth" : 1701.8 * mm});
        }
        {
            var Q0;
            Q0=makeQuery(id+"F1.opExtrude","CAP_FACE",FACE,{"disambiguationData":[OSD([sQuery(id+"F0.wireOp",EDGE,"E0.bottom"),sQuery(id+"F0.wireOp",EDGE,"E0.top"),sQuery(id+"F0.wireOp",EDGE,"E0.left"),sQuery(id+"F0.wireOp",EDGE,"E0.right")])],"isStart":true});
            var sketch = newSketch(context, id + "F22", { "sketchPlane" : qUnion([Q0])});
            skLineSegment(sketch, "E215.bottom", {"start": v(6096, -1117.6) * mm, "end": v(6121.4, -1117.6) * mm});
            skLineSegment(sketch, "E215.top", {"start": v(6096, -3403.6) * mm, "end": v(6121.4, -3403.6) * mm});
            skLineSegment(sketch, "E215.left", {"start": v(6096, -1117.6) * mm, "end": v(6096, -3403.6) * mm});
            skLineSegment(sketch, "E215.right", {"start": v(6121.4, -1117.6) * mm, "end": v(6121.4, -3403.6) * mm});
            skLineSegment(sketch, "E216.bottom", {"start": v(11582.4, -1117.6) * mm, "end": v(11557, -1117.6) * mm});
            skLineSegment(sketch, "E216.top", {"start": v(11582.4, -3403.6) * mm, "end": v(11557, -3403.6) * mm});
            skLineSegment(sketch, "E216.left", {"start": v(11582.4, -1117.6) * mm, "end": v(11582.4, -3403.6) * mm});
            skLineSegment(sketch, "E216.right", {"start": v(11557, -1117.6) * mm, "end": v(11557, -3403.6) * mm});
            skLineSegment(sketch, "E217.bottom", {"start": v(0, -10464.8) * mm, "end": v(2286, -10464.8) * mm});
            skLineSegment(sketch, "E217.top", {"start": v(0, -10439.4) * mm, "end": v(2286, -10439.4) * mm});
            skLineSegment(sketch, "E217.left", {"start": v(0, -10464.8) * mm, "end": v(0, -10439.4) * mm});
            skLineSegment(sketch, "E217.right", {"start": v(2286, -10464.8) * mm, "end": v(2286, -10439.4) * mm});
            skLineSegment(sketch, "E218.bottom", {"start": v(0, -13335) * mm, "end": v(2286, -13335) * mm});
            skLineSegment(sketch, "E218.top", {"start": v(0, -13309.6) * mm, "end": v(2286, -13309.6) * mm});
            skLineSegment(sketch, "E218.left", {"start": v(0, -13335) * mm, "end": v(0, -13309.6) * mm});
            skLineSegment(sketch, "E218.right", {"start": v(2286, -13335) * mm, "end": v(2286, -13309.6) * mm});
            skSolve(sketch);
        }
        {
            var Q0;
            Q0 = qSketchRegion(id + "F22", true);
            extrude(context, id + "F23", {"entities" : qUnion([Q0]), "depth" : 2489.2 * mm});
        }
        {
            var Q0;
            Q0=makeQuery(id+"F1.opExtrude","CAP_FACE",FACE,{"disambiguationData":[OSD([sQuery(id+"F0.wireOp",EDGE,"E0.bottom"),sQuery(id+"F0.wireOp",EDGE,"E0.top"),sQuery(id+"F0.wireOp",EDGE,"E0.left"),sQuery(id+"F0.wireOp",EDGE,"E0.right")])],"isStart":true});
            var sketch = newSketch(context, id + "F24", { "sketchPlane" : qUnion([Q0])});
            skLineSegment(sketch, "E219.bottom", {"start": v(10871.2, -17475.2) * mm, "end": v(12674.6, -17475.2) * mm});
            skLineSegment(sketch, "E219.top", {"start": v(10871.2, -18237.2) * mm, "end": v(12674.6, -18237.2) * mm});
            skLineSegment(sketch, "E219.left", {"start": v(10871.2, -17475.2) * mm, "end": v(10871.2, -18237.2) * mm});
            skLineSegment(sketch, "E219.right", {"start": v(12674.6, -17475.2) * mm, "end": v(12674.6, -18237.2) * mm});
            skSolve(sketch);
        }
        {
            var Q0;
            Q0 = qSketchRegion(id + "F24", true);
            extrude(context, id + "F25", {"entities" : qUnion([Q0]), "depth" : 1574.8 * mm});
        }
        {
            var Q0;
            Q0=makeQuery(id+"F1.opExtrude","CAP_FACE",FACE,{"disambiguationData":[OSD([sQuery(id+"F0.wireOp",EDGE,"E0.bottom"),sQuery(id+"F0.wireOp",EDGE,"E0.top"),sQuery(id+"F0.wireOp",EDGE,"E0.left"),sQuery(id+"F0.wireOp",EDGE,"E0.right")])],"isStart":true});
            var sketch = newSketch(context, id + "F26", { "sketchPlane" : qUnion([Q0])});
            skLineSegment(sketch, "E220.bottom", {"start": v(7531.1, -17526) * mm, "end": v(9359.9, -17526) * mm});
            skLineSegment(sketch, "E220.top", {"start": v(7531.1, -18288) * mm, "end": v(9359.9, -18288) * mm});
            skLineSegment(sketch, "E220.left", {"start": v(7531.1, -17526) * mm, "end": v(7531.1, -18288) * mm});
            skLineSegment(sketch, "E220.right", {"start": v(9359.9, -17526) * mm, "end": v(9359.9, -18288) * mm});
            skSolve(sketch);
        }
        {
            var Q0;
            Q0 = qSketchRegion(id + "F26", true);
            extrude(context, id + "F27", {"entities" : qUnion([Q0]), "depth" : 1219.2 * mm});
        }
        {
            var Q0;
            Q0=makeQuery(id+"F1.opExtrude","CAP_FACE",FACE,{"disambiguationData":[OSD([sQuery(id+"F0.wireOp",EDGE,"E0.bottom"),sQuery(id+"F0.wireOp",EDGE,"E0.top"),sQuery(id+"F0.wireOp",EDGE,"E0.left"),sQuery(id+"F0.wireOp",EDGE,"E0.right")])],"isStart":true});
            var sketch = newSketch(context, id + "F28", { "sketchPlane" : qUnion([Q0])});
            skLineSegment(sketch, "E221", {"start": v(1701.8, -6477) * mm, "end": v(533.4, -6477) * mm});
            skLineSegment(sketch, "E222", {"start": v(533.4, -6477) * mm, "end": v(533.4, -5562.6) * mm});
            skLineSegment(sketch, "E223", {"start": v(533.4, -5562.6) * mm, "end": v(1701.8, -5562.6) * mm});
            skLineSegment(sketch, "E224", {"start": v(1701.8, -5562.6) * mm, "end": v(1701.8, -5105.4) * mm});
            skLineSegment(sketch, "E225", {"start": v(1701.8, -5105.4) * mm, "end": v(1955.8, -5105.4) * mm});
            skLineSegment(sketch, "E226", {"start": v(1955.8, -5105.4) * mm, "end": v(1955.8, -5562.6) * mm});
            skLineSegment(sketch, "E227", {"start": v(1955.8, -5562.6) * mm, "end": v(2159, -5562.6) * mm});
            skLineSegment(sketch, "E228", {"start": v(2159, -5562.6) * mm, "end": v(2159, -6477) * mm});
            skLineSegment(sketch, "E229", {"start": v(2159, -6477) * mm, "end": v(1955.8, -6477) * mm});
            skLineSegment(sketch, "E230", {"start": v(1955.8, -6477) * mm, "end": v(1955.8, -6934.2) * mm});
            skLineSegment(sketch, "E231", {"start": v(1955.8, -6934.2) * mm, "end": v(1701.8, -6934.2) * mm});
            skLineSegment(sketch, "E232", {"start": v(1701.8, -6934.2) * mm, "end": v(1701.8, -6477) * mm});
            skLineSegment(sketch, "E233", {"start": v(533.4, -9664.7) * mm, "end": v(533.4, -8521.7) * mm});
            skLineSegment(sketch, "E234", {"start": v(533.4, -8521.7) * mm, "end": v(1701.8, -8521.7) * mm});
            skLineSegment(sketch, "E235", {"start": v(1701.8, -8521.7) * mm, "end": v(1701.8, -8178.8) * mm});
            skLineSegment(sketch, "E236", {"start": v(1701.8, -8178.8) * mm, "end": v(1955.8, -8178.8) * mm});
            skLineSegment(sketch, "E237", {"start": v(1955.8, -8178.8) * mm, "end": v(1955.8, -8521.7) * mm});
            skLineSegment(sketch, "E238", {"start": v(1955.8, -8521.7) * mm, "end": v(2159, -8521.7) * mm});
            skLineSegment(sketch, "E239", {"start": v(2159, -8521.7) * mm, "end": v(2159, -9664.7) * mm});
            skLineSegment(sketch, "E240", {"start": v(2159, -9664.7) * mm, "end": v(1955.8, -9664.7) * mm});
            skLineSegment(sketch, "E241", {"start": v(1955.8, -9664.7) * mm, "end": v(1955.8, -10007.6) * mm});
            skLineSegment(sketch, "E242", {"start": v(1955.8, -10007.6) * mm, "end": v(1701.8, -10007.6) * mm});
            skLineSegment(sketch, "E243", {"start": v(1701.8, -10007.6) * mm, "end": v(1701.8, -9664.7) * mm});
            skLineSegment(sketch, "E244", {"start": v(1701.8, -9664.7) * mm, "end": v(533.4, -9664.7) * mm});
            skLineSegment(sketch, "E245", {"start": v(2159, -6019.8) * mm, "end": v(533.4, -6019.8) * mm, "construction": true});
            skLineSegment(sketch, "E246", {"start": v(2159, -9093.2) * mm, "end": v(533.4, -9093.2) * mm, "construction": true});
            skSolve(sketch);
        }
        {
            var Q0;
            Q0 = qSketchRegion(id + "F28", true);
            extrude(context, id + "F29", {"entities" : qUnion([Q0]), "depth" : 2362.2 * mm});
        }
        {
            var Q0;
            Q0=makeQuery(id+"F1.opExtrude","CAP_FACE",FACE,{"disambiguationData":[OSD([sQuery(id+"F0.wireOp",EDGE,"E0.bottom"),sQuery(id+"F0.wireOp",EDGE,"E0.top"),sQuery(id+"F0.wireOp",EDGE,"E0.left"),sQuery(id+"F0.wireOp",EDGE,"E0.right")])],"isStart":true});
            var sketch = newSketch(context, id + "F30", { "sketchPlane" : qUnion([Q0])});
            skLineSegment(sketch, "E247.bottom", {"start": v(939.8, -13716) * mm, "end": v(2286, -13716) * mm});
            skLineSegment(sketch, "E247.top", {"start": v(939.8, -15544.8) * mm, "end": v(2286, -15544.8) * mm});
            skLineSegment(sketch, "E247.left", {"start": v(939.8, -13716) * mm, "end": v(939.8, -15544.8) * mm});
            skLineSegment(sketch, "E247.right", {"start": v(2286, -13716) * mm, "end": v(2286, -15544.8) * mm});
            skLineSegment(sketch, "E248.bottom", {"start": v(609.6, -16357.6) * mm, "end": v(2286, -16357.6) * mm});
            skLineSegment(sketch, "E248.top", {"start": v(609.6, -18491.2) * mm, "end": v(2286, -18491.2) * mm});
            skLineSegment(sketch, "E248.left", {"start": v(609.6, -16357.6) * mm, "end": v(609.6, -18491.2) * mm});
            skLineSegment(sketch, "E248.right", {"start": v(2286, -16357.6) * mm, "end": v(2286, -18491.2) * mm});
            skSolve(sketch);
        }
        {
            var Q0;
            Q0 = qSketchRegion(id + "F30", true);
            extrude(context, id + "F31", {"entities" : qUnion([Q0]), "depth" : 1981.2 * mm});
        }
        {
            var Q0;
            Q0=makeQuery(id+"F3.opExtrude","CAP_FACE",FACE,{"disambiguationData":[OSD([sQuery(id+"F2.wireOp",EDGE,"E1.bottom"),sQuery(id+"F2.wireOp",EDGE,"E1.left"),sQuery(id+"F2.wireOp",EDGE,"E2.top"),sQuery(id+"F2.wireOp",EDGE,"E2.left"),sQuery(id+"F2.wireOp",EDGE,"E2.right"),sQuery(id+"F2.wireOp",EDGE,"E8"),sQuery(id+"F2.wireOp",EDGE,"E9"),sQuery(id+"F2.wireOp",EDGE,"E10"),sQuery(id+"F2.wireOp",EDGE,"E11"),sQuery(id+"F2.wireOp",EDGE,"E12"),sQuery(id+"F2.wireOp",EDGE,"E31"),sQuery(id+"F2.wireOp",EDGE,"E32"),sQuery(id+"F2.wireOp",EDGE,"E33"),sQuery(id+"F2.wireOp",EDGE,"E34"),sQuery(id+"F2.wireOp",EDGE,"E35"),sQuery(id+"F2.wireOp",EDGE,"E43"),sQuery(id+"F2.wireOp",EDGE,"E45.trimOffspring"),sQuery(id+"F2.wireOp",EDGE,"E55"),sQuery(id+"F2.wireOp",EDGE,"E56"),sQuery(id+"F2.wireOp",EDGE,"E59"),sQuery(id+"F2.wireOp",EDGE,"E60"),sQuery(id+"F2.wireOp",EDGE,"E62.trimOffspring"),sQuery(id+"F2.wireOp",EDGE,"E64.trimOffspring"),sQuery(id+"F2.wireOp",EDGE,"E66.trimOffspring"),sQuery(id+"F2.wireOp",EDGE,"E67"),sQuery(id+"F2.wireOp",EDGE,"E69"),sQuery(id+"F2.wireOp",EDGE,"E71")])],"isStart":false});
            var sketch = newSketch(context, id + "F32", { "sketchPlane" : qUnion([Q0])});
            skLineSegment(sketch, "E249.bottom", {"start": v(15113, 292.1) * mm, "end": v(-292.1, 292.1) * mm});
            skLineSegment(sketch, "E249.top", {"start": v(15113, -19494.5) * mm, "end": v(-292.1, -19494.5) * mm});
            skLineSegment(sketch, "E249.left", {"start": v(15113, 292.1) * mm, "end": v(15113, -19494.5) * mm});
            skLineSegment(sketch, "E249.right", {"start": v(-292.1, 292.1) * mm, "end": v(-292.1, -19494.5) * mm});
            skLineSegment(sketch, "E250.bottom", {"start": v(6972.3, -14224) * mm, "end": v(9372.6, -14224) * mm});
            skLineSegment(sketch, "E250.top", {"start": v(6972.3, -17246.6) * mm, "end": v(9372.6, -17246.6) * mm});
            skLineSegment(sketch, "E250.left", {"start": v(6972.3, -14224) * mm, "end": v(6972.3, -17246.6) * mm});
            skLineSegment(sketch, "E250.right", {"start": v(9372.6, -14224) * mm, "end": v(9372.6, -17246.6) * mm});
            skLineSegment(sketch, "E251.bottom", {"start": v(6972.3, -9067.8) * mm, "end": v(9067.8, -9067.8) * mm});
            skLineSegment(sketch, "E251.top", {"start": v(6972.3, -12674.6) * mm, "end": v(9067.8, -12674.6) * mm});
            skLineSegment(sketch, "E251.left", {"start": v(6972.3, -9067.8) * mm, "end": v(6972.3, -12674.6) * mm});
            skLineSegment(sketch, "E251.right", {"start": v(9067.8, -9067.8) * mm, "end": v(9067.8, -12674.6) * mm});
            skSolve(sketch);
        }
        {
            var Q0;
            Q0 = qSketchRegion(id + "F32", true);
            extrude(context, id + "F33", {"entities" : qUnion([Q0]), "depth" : 609.6 * mm});
        }
        {
            var Q0;
            Q0=makeQuery(id+"F1.opExtrude","CAP_FACE",FACE,{"disambiguationData":[OSD([sQuery(id+"F0.wireOp",EDGE,"E0.bottom"),sQuery(id+"F0.wireOp",EDGE,"E0.top"),sQuery(id+"F0.wireOp",EDGE,"E0.left"),sQuery(id+"F0.wireOp",EDGE,"E0.right")])],"isStart":true});
            var sketch = newSketch(context, id + "F34", { "sketchPlane" : qUnion([Q0])});
            skLineSegment(sketch, "E252.bottom", {"start": v(5665.72, -9392.26) * mm, "end": v(10364.72, -9392.26) * mm});
            skLineSegment(sketch, "E252.top", {"start": v(6491.22, -12338.66) * mm, "end": v(8828.02, -12338.66) * mm});
            skLineSegment(sketch, "E252.left", {"start": v(5665.72, -9392.26) * mm, "end": v(5665.72, -12135.46) * mm});
            skLineSegment(sketch, "E252.right", {"start": v(10364.72, -9392.26) * mm, "end": v(10364.72, -11729.06) * mm});
            skLineSegment(sketch, "E253", {"start": v(8015.22, -9392.26) * mm, "end": v(8015.22, -12338.66) * mm, "construction": true});
            skLineSegment(sketch, "E254", {"start": v(9132.82, -9392.26) * mm, "end": v(9132.82, -11729.06) * mm, "construction": true});
            skLineSegment(sketch, "E255", {"start": v(6897.62, -9392.26) * mm, "end": v(6897.62, -12338.66) * mm, "construction": true});
            skLineSegment(sketch, "E256", {"start": v(5665.72, -12135.46) * mm, "end": v(6491.22, -12135.46) * mm});
            skLineSegment(sketch, "E257", {"start": v(6491.22, -12135.46) * mm, "end": v(6491.22, -12338.66) * mm});
            skLineSegment(sketch, "E258", {"start": v(10364.72, -11729.06) * mm, "end": v(8828.02, -11729.06) * mm});
            skLineSegment(sketch, "E259", {"start": v(8828.02, -11729.06) * mm, "end": v(8828.02, -12338.66) * mm});
            skPoint(sketch, "E260.orphan", {"position": v(10364.72, -12338.66) * mm});
            skPoint(sketch, "E261.orphan", {"position": v(5665.72, -12338.66) * mm});
            skSolve(sketch);
        }
        {
            var Q0;
            Q0 = qSketchRegion(id + "F34", true);
            extrude(context, id + "F35", {"entities" : qUnion([Q0]), "depth" : 2438.4 * mm});
        }
        {
            var Q0;
            Q0=makeQuery(id+"F35.opExtrude","CAP_FACE",FACE,{"disambiguationData":[OSD([sQuery(id+"F34.wireOp",EDGE,"E252.bottom"),sQuery(id+"F34.wireOp",EDGE,"E252.top"),sQuery(id+"F34.wireOp",EDGE,"E252.left"),sQuery(id+"F34.wireOp",EDGE,"E252.right"),sQuery(id+"F34.wireOp",EDGE,"E256"),sQuery(id+"F34.wireOp",EDGE,"E257"),sQuery(id+"F34.wireOp",EDGE,"E258"),sQuery(id+"F34.wireOp",EDGE,"E259")])],"isStart":false});
            var sketch = newSketch(context, id + "F36", { "sketchPlane" : qUnion([Q0])});
            skLineSegment(sketch, "E262.bottom", {"start": v(7761.22, -10382.86) * mm, "end": v(8269.22, -10382.86) * mm});
            skLineSegment(sketch, "E262.left", {"start": v(8269.22, -11144.86) * mm, "end": v(8269.22, -10382.86) * mm});
            skLineSegment(sketch, "E262.right", {"start": v(7761.22, -11144.86) * mm, "end": v(7761.22, -10382.86) * mm});
            skLineSegment(sketch, "E263", {"start": v(8269.22, -11144.86) * mm, "end": v(8474.52, -11500.46) * mm});
            skLineSegment(sketch, "E264", {"start": v(7555.91, -11500.46) * mm, "end": v(8474.52, -11500.46) * mm});
            skLineSegment(sketch, "E265", {"start": v(7555.91, -11500.46) * mm, "end": v(7761.22, -11144.86) * mm});
            skLineSegment(sketch, "E266", {"start": v(8015.22, -9392.26) * mm, "end": v(8015.22, -10382.86) * mm, "construction": true});
            skSolve(sketch);
        }
        {
            var Q0;
            Q0 = qSketchRegion(id + "F36", true);
            extrude(context, id + "F37", {"entities" : qUnion([Q0]), "operationType" : NewBodyOperationType.ADD, "depth" : 939.8 * mm});
        }
        {
            var Q0;
            Q0=makeQuery(id+"F37.opExtrude","SWEPT_FACE",FACE,{"disambiguationData":[OSD([sQuery(id+"F36.wireOp",EDGE,"E262.right")])]});
            var sketch = newSketch(context, id + "F38", { "sketchPlane" : qUnion([Q0])});
            skCircle(sketch, "E267", {"center": v(10738.46, 2395.22) * mm, "radius": 342.9 * mm});
            skPoint(sketch, "E268", {"position": v(10738.46, 2738.12) * mm});
            skSolve(sketch);
        }
        {
            var Q0;
            Q0 = qSketchRegion(id + "F38", true);
            extrude(context, id + "F39", {"entities" : qUnion([Q0]), "operationType" : NewBodyOperationType.ADD, "oppositeDirection" : true, "depth" : 1028.7 * mm});
        }
        {
            var Q0;
            Q0=makeQuery(id+"F1.opExtrude","CAP_FACE",FACE,{"disambiguationData":[OSD([sQuery(id+"F0.wireOp",EDGE,"E0.bottom"),sQuery(id+"F0.wireOp",EDGE,"E0.top"),sQuery(id+"F0.wireOp",EDGE,"E0.left"),sQuery(id+"F0.wireOp",EDGE,"E0.right")])],"isStart":true});
            var sketch = newSketch(context, id + "F40", { "sketchPlane" : qUnion([Q0])});
            skLineSegment(sketch, "E269.bottom", {"start": v(11385.55, -12903.2) * mm, "end": v(12122.15, -12903.2) * mm});
            skLineSegment(sketch, "E269.top", {"start": v(11385.55, -13919.2) * mm, "end": v(12122.15, -13919.2) * mm});
            skLineSegment(sketch, "E269.left", {"start": v(11385.55, -12903.2) * mm, "end": v(11385.55, -13919.2) * mm});
            skLineSegment(sketch, "E269.right", {"start": v(12122.15, -12903.2) * mm, "end": v(12122.15, -13919.2) * mm});
            skSolve(sketch);
        }
        {
            var Q0;
            Q0 = qSketchRegion(id + "F40", true);
            extrude(context, id + "F41", {"entities" : qUnion([Q0]), "depth" : 1651 * mm});
        }
        {
            var Q0;
            Q0=makeQuery(id+"F1.opExtrude","CAP_FACE",FACE,{"disambiguationData":[OSD([sQuery(id+"F0.wireOp",EDGE,"E0.bottom"),sQuery(id+"F0.wireOp",EDGE,"E0.top"),sQuery(id+"F0.wireOp",EDGE,"E0.left"),sQuery(id+"F0.wireOp",EDGE,"E0.right")])],"isStart":true});
            var sketch = newSketch(context, id + "F42", { "sketchPlane" : qUnion([Q0])});
            skLineSegment(sketch, "E270.bottom", {"start": v(10725.15, -7518.4) * mm, "end": v(12528.55, -7518.4) * mm});
            skLineSegment(sketch, "E270.top", {"start": v(10725.15, -8229.6) * mm, "end": v(12528.55, -8229.6) * mm});
            skLineSegment(sketch, "E270.left", {"start": v(10725.15, -7518.4) * mm, "end": v(10725.15, -8229.6) * mm});
            skLineSegment(sketch, "E270.right", {"start": v(12528.55, -7518.4) * mm, "end": v(12528.55, -8229.6) * mm});
            skLineSegment(sketch, "E271", {"start": v(11626.85, -7518.4) * mm, "end": v(11626.85, -1422.4) * mm, "construction": true});
            skSolve(sketch);
        }
        {
            var Q0;
            Q0 = qSketchRegion(id + "F42", true);
            extrude(context, id + "F43", {"entities" : qUnion([Q0]), "depth" : 1117.6 * mm});
        }
        {
            var Q0;
            Q0=makeQuery(id+"F35.opExtrude","SWEPT_FACE",FACE,{"disambiguationData":[OSD([sQuery(id+"F34.wireOp",EDGE,"E252.right")])]});
            var sketch = newSketch(context, id + "F44", { "sketchPlane" : qUnion([Q0])});
            skLineSegment(sketch, "E272.bottom", {"start": v(-9392.26, 2438.4) * mm, "end": v(-10154.26, 2438.4) * mm});
            skLineSegment(sketch, "E272.top", {"start": v(-9392.26, 2171.7) * mm, "end": v(-10154.26, 2171.7) * mm});
            skLineSegment(sketch, "E272.left", {"start": v(-9392.26, 2438.4) * mm, "end": v(-9392.26, 2171.7) * mm});
            skLineSegment(sketch, "E272.right", {"start": v(-10154.26, 2438.4) * mm, "end": v(-10154.26, 2171.7) * mm});
            skSolve(sketch);
        }
        {
            var Q0;
            Q0 = qSketchRegion(id + "F44", true);
            var Q1;
            Q1=makeQuery(id+"F35.opExtrude","SWEPT_FACE",FACE,{"disambiguationData":[OSD([sQuery(id+"F34.wireOp",EDGE,"E252.left")])]});
            extrude(context, id + "F45", {"entities" : qUnion([Q0]), "operationType" : NewBodyOperationType.REMOVE, "endBound" : BoundingType.UP_TO_SURFACE, "oppositeDirection" : true, "endBoundEntityFace" : qUnion([Q1]), "depth" : 25.4 * mm});
        }
        {
            var Q0;
            Q0=makeQuery(id+"F35.opExtrude","CAP_FACE",FACE,{"disambiguationData":[OSD([sQuery(id+"F34.wireOp",EDGE,"E252.bottom"),sQuery(id+"F34.wireOp",EDGE,"E252.top"),sQuery(id+"F34.wireOp",EDGE,"E252.left"),sQuery(id+"F34.wireOp",EDGE,"E252.right"),sQuery(id+"F34.wireOp",EDGE,"E256"),sQuery(id+"F34.wireOp",EDGE,"E257"),sQuery(id+"F34.wireOp",EDGE,"E258"),sQuery(id+"F34.wireOp",EDGE,"E259")])],"isStart":false});
            var sketch = newSketch(context, id + "F46", { "sketchPlane" : qUnion([Q0])});
            skPoint(sketch, "E273.firstSnap0", {"position": v(8015.22, -11500.46) * mm});
            skLineSegment(sketch, "E273.bottom", {"start": v(7202.42, -11500.46) * mm, "end": v(8828.02, -11500.46) * mm});
            skLineSegment(sketch, "E273.top", {"start": v(7202.42, -12338.66) * mm, "end": v(8828.02, -12338.66) * mm});
            skLineSegment(sketch, "E273.left", {"start": v(7202.42, -11500.46) * mm, "end": v(7202.42, -12338.66) * mm});
            skLineSegment(sketch, "E273.right", {"start": v(8828.02, -11500.46) * mm, "end": v(8828.02, -12338.66) * mm});
            skSolve(sketch);
        }
        {
            var Q0;
            Q0 = qSketchRegion(id + "F46", true);
            extrude(context, id + "F47", {"entities" : qUnion([Q0]), "operationType" : NewBodyOperationType.ADD, "depth" : 254 * mm});
        }
        {
            var Q0;
            Q0=makeQuery(id+"F35.opExtrude","SWEPT_FACE",FACE,{"disambiguationData":[OSD([sQuery(id+"F34.wireOp",EDGE,"E258")])]});
            var sketch = newSketch(context, id + "F48", { "sketchPlane" : qUnion([Q0])});
            skLineSegment(sketch, "E274.bottom", {"start": v(10364.72, 0) * mm, "end": v(9094.72, 0) * mm});
            skLineSegment(sketch, "E274.top", {"start": v(10364.72, 457.2) * mm, "end": v(9094.72, 457.2) * mm});
            skLineSegment(sketch, "E274.left", {"start": v(10364.72, 0) * mm, "end": v(10364.72, 457.2) * mm});
            skLineSegment(sketch, "E274.right", {"start": v(9094.72, 0) * mm, "end": v(9094.72, 457.2) * mm});
            skSolve(sketch);
        }
        {
            var Q0;
            Q0 = qSketchRegion(id + "F48", true);
            extrude(context, id + "F49", {"entities" : qUnion([Q0]), "depth" : 838.2 * mm});
        }
        {
            var Q0;
            Q0=makeQuery(id+"F35.opExtrude","SWEPT_FACE",FACE,{"disambiguationData":[OSD([sQuery(id+"F34.wireOp",EDGE,"E252.right")])]});
            var sketch = newSketch(context, id + "F50", { "sketchPlane" : qUnion([Q0])});
            skLineSegment(sketch, "E275.bottom", {"start": v(-9392.26, 0) * mm, "end": v(-9951.06, 0) * mm});
            skLineSegment(sketch, "E275.top", {"start": v(-9392.26, 1219.2) * mm, "end": v(-9951.06, 1219.2) * mm});
            skLineSegment(sketch, "E275.left", {"start": v(-9392.26, 0) * mm, "end": v(-9392.26, 1219.2) * mm});
            skLineSegment(sketch, "E275.right", {"start": v(-9951.06, 0) * mm, "end": v(-9951.06, 1219.2) * mm});
            skSolve(sketch);
        }
        {
            var Q0;
            Q0 = qSketchRegion(id + "F50", true);
            extrude(context, id + "F51", {"entities" : qUnion([Q0]), "depth" : 406.4 * mm});
        }
        {
            var Q0;
            Q0=makeQuery(id+"F1.opExtrude","CAP_FACE",FACE,{"disambiguationData":[OSD([sQuery(id+"F0.wireOp",EDGE,"E0.bottom"),sQuery(id+"F0.wireOp",EDGE,"E0.top"),sQuery(id+"F0.wireOp",EDGE,"E0.left"),sQuery(id+"F0.wireOp",EDGE,"E0.right")])],"isStart":true});
            var sketch = newSketch(context, id + "F52", { "sketchPlane" : qUnion([Q0])});
            skLineSegment(sketch, "E276", {"start": v(29603.7, -1117.6) * mm, "end": v(29603.7, -4064) * mm});
            skLineSegment(sketch, "E277", {"start": v(29603.7, -4064) * mm, "end": v(31635.7, -4064) * mm});
            skLineSegment(sketch, "E278", {"start": v(31635.7, -4064) * mm, "end": v(31635.7, -3962.4) * mm});
            skLineSegment(sketch, "E279", {"start": v(31635.7, -3962.4) * mm, "end": v(29705.3, -3962.4) * mm});
            skLineSegment(sketch, "E280", {"start": v(29705.3, -3962.4) * mm, "end": v(29705.3, -1117.6) * mm});
            skLineSegment(sketch, "E281", {"start": v(29705.3, -1117.6) * mm, "end": v(29603.7, -1117.6) * mm});
            skSolve(sketch);
        }
        {
            var Q0;
            Q0 = qSketchRegion(id + "F52", true);
            extrude(context, id + "F53", {"entities" : qUnion([Q0]), "depth" : 1828.8 * mm});
        }
        {
            var Q0;
            Q0=makeQuery(id+"F1.opExtrude","CAP_FACE",FACE,{"disambiguationData":[OSD([sQuery(id+"F0.wireOp",EDGE,"E0.bottom"),sQuery(id+"F0.wireOp",EDGE,"E0.top"),sQuery(id+"F0.wireOp",EDGE,"E0.left"),sQuery(id+"F0.wireOp",EDGE,"E0.right")])],"isStart":true});
            var sketch = newSketch(context, id + "F54", { "sketchPlane" : qUnion([Q0])});
            skLineSegment(sketch, "E282", {"start": v(23964.9, 0) * mm, "end": v(23964.9, -1803.4) * mm});
            skLineSegment(sketch, "E283", {"start": v(23964.9, -1803.4) * mm, "end": v(24574.5, -1803.4) * mm});
            skLineSegment(sketch, "E284", {"start": v(24574.5, -1803.4) * mm, "end": v(24574.5, -1193.8) * mm});
            skLineSegment(sketch, "E285", {"start": v(24574.5, -1193.8) * mm, "end": v(24422.1, -1193.8) * mm});
            skLineSegment(sketch, "E286", {"start": v(24422.1, -1193.8) * mm, "end": v(24422.1, 0) * mm});
            skLineSegment(sketch, "E287", {"start": v(24422.1, 0) * mm, "end": v(23964.9, 0) * mm});
            skSolve(sketch);
        }
        {
            var Q0;
            Q0 = qSketchRegion(id + "F54", true);
            extrude(context, id + "F55", {"entities" : qUnion([Q0]), "depth" : 914.4 * mm});
        }
        {
            var Q0;
            Q0=makeQuery(id+"F1.opExtrude","CAP_FACE",FACE,{"disambiguationData":[OSD([sQuery(id+"F0.wireOp",EDGE,"E0.bottom"),sQuery(id+"F0.wireOp",EDGE,"E0.top"),sQuery(id+"F0.wireOp",EDGE,"E0.left"),sQuery(id+"F0.wireOp",EDGE,"E0.right")])],"isStart":true});
            var sketch = newSketch(context, id + "F56", { "sketchPlane" : qUnion([Q0])});
            skLineSegment(sketch, "E288", {"start": v(27470.1, -15760.7) * mm, "end": v(27470.1, -13728.7) * mm});
            skLineSegment(sketch, "E289", {"start": v(27470.1, -12407.9) * mm, "end": v(31635.7, -12407.9) * mm});
            skLineSegment(sketch, "E290", {"start": v(31635.7, -12407.9) * mm, "end": v(31635.7, -12522.2) * mm});
            skLineSegment(sketch, "E291", {"start": v(31635.7, -12522.2) * mm, "end": v(27584.4, -12522.2) * mm});
            skLineSegment(sketch, "E292", {"start": v(27584.4, -12522.2) * mm, "end": v(27584.4, -12712.7) * mm});
            skLineSegment(sketch, "E293", {"start": v(27584.4, -15760.7) * mm, "end": v(27470.1, -15760.7) * mm});
            skLineSegment(sketch, "E294", {"start": v(27470.1, -12712.7) * mm, "end": v(27584.4, -12712.7) * mm});
            skLineSegment(sketch, "E295", {"start": v(27584.4, -13728.7) * mm, "end": v(27470.1, -13728.7) * mm});
            skLineSegment(sketch, "E296.trimOffspring", {"start": v(27470.1, -12712.7) * mm, "end": v(27470.1, -12407.9) * mm});
            skLineSegment(sketch, "E297.trimOffspring", {"start": v(27584.4, -13728.7) * mm, "end": v(27584.4, -15760.7) * mm});
            skSolve(sketch);
        }
        {
            var Q0;
            Q0 = qSketchRegion(id + "F56", true);
            extrude(context, id + "F57", {"entities" : qUnion([Q0]), "depth" : 2921 * mm});
        }
        {
            var Q0;
            Q0=makeQuery(id+"F57.opExtrude","CAP_FACE",FACE,{"disambiguationData":[OSD([sQuery(id+"F56.wireOp",EDGE,"E289"),sQuery(id+"F56.wireOp",EDGE,"E290"),sQuery(id+"F56.wireOp",EDGE,"E291"),sQuery(id+"F56.wireOp",EDGE,"E292"),sQuery(id+"F56.wireOp",EDGE,"E294"),sQuery(id+"F56.wireOp",EDGE,"E296.trimOffspring")])],"isStart":false});
            var sketch = newSketch(context, id + "F58", { "sketchPlane" : qUnion([Q0])});
            skLineSegment(sketch, "E298", {"start": v(27470.1, -12712.7) * mm, "end": v(27470.1, -13728.7) * mm});
            skLineSegment(sketch, "E299", {"start": v(27470.1, -13728.7) * mm, "end": v(27584.4, -13728.7) * mm});
            skLineSegment(sketch, "E300", {"start": v(27584.4, -13728.7) * mm, "end": v(27584.4, -12712.7) * mm});
            skLineSegment(sketch, "E301", {"start": v(27470.1, -12712.7) * mm, "end": v(27584.4, -12712.7) * mm});
            skSolve(sketch);
        }
        {
            var Q0;
            Q0 = qSketchRegion(id + "F58", true);
            extrude(context, id + "F59", {"entities" : qUnion([Q0]), "oppositeDirection" : true, "depth" : 736.6 * mm});
        }
        {
            var Q0;
            Q0=makeQuery(id+"F57.opExtrude","SWEPT_FACE",FACE,{"disambiguationData":[OSD([sQuery(id+"F56.wireOp",EDGE,"E291")])]});
            var sketch = newSketch(context, id + "F60", { "sketchPlane" : qUnion([Q0])});
            skLineSegment(sketch, "E302.bottom", {"start": v(28384.5, 2133.6) * mm, "end": v(29603.7, 2133.6) * mm});
            skLineSegment(sketch, "E302.top", {"start": v(28384.5, 914.4) * mm, "end": v(29603.7, 914.4) * mm});
            skLineSegment(sketch, "E302.left", {"start": v(28384.5, 2133.6) * mm, "end": v(28384.5, 914.4) * mm});
            skLineSegment(sketch, "E302.right", {"start": v(29603.7, 2133.6) * mm, "end": v(29603.7, 914.4) * mm});
            skSolve(sketch);
        }
        {
            var Q0;
            Q0 = qSketchRegion(id + "F60", true);
            extrude(context, id + "F61", {"entities" : qUnion([Q0]), "operationType" : NewBodyOperationType.REMOVE, "oppositeDirection" : true, "depth" : 203.2 * mm});
        }
        {
            var Q0;
            Q0=makeQuery(id+"F1.opExtrude","CAP_FACE",FACE,{"disambiguationData":[OSD([sQuery(id+"F0.wireOp",EDGE,"E0.bottom"),sQuery(id+"F0.wireOp",EDGE,"E0.top"),sQuery(id+"F0.wireOp",EDGE,"E0.left"),sQuery(id+"F0.wireOp",EDGE,"E0.right")])],"isStart":true});
            var sketch = newSketch(context, id + "F62", { "sketchPlane" : qUnion([Q0])});
            skLineSegment(sketch, "E303.bottom", {"start": v(9448.8, 0) * mm, "end": v(11582.4, 0) * mm});
            skLineSegment(sketch, "E303.top", {"start": v(9448.8, -1524) * mm, "end": v(11582.4, -1524) * mm});
            skLineSegment(sketch, "E303.left", {"start": v(9448.8, 0) * mm, "end": v(9448.8, -1524) * mm});
            skLineSegment(sketch, "E303.right", {"start": v(11582.4, 0) * mm, "end": v(11582.4, -1524) * mm});
            skLineSegment(sketch, "E304.bottom", {"start": v(6254.33, -362.79) * mm, "end": v(6863.93, -362.79) * mm});
            skLineSegment(sketch, "E304.top", {"start": v(6254.33, -1277.19) * mm, "end": v(6863.93, -1277.19) * mm});
            skLineSegment(sketch, "E304.left", {"start": v(6254.33, -362.79) * mm, "end": v(6254.33, -1277.19) * mm});
            skLineSegment(sketch, "E304.right", {"start": v(6863.93, -362.79) * mm, "end": v(6863.93, -1277.19) * mm});
            skLineSegment(sketch, "E305.bottom", {"start": v(7066.94, -751.8) * mm, "end": v(7524.14, -751.8) * mm});
            skLineSegment(sketch, "E305.top", {"start": v(7066.94, -1209) * mm, "end": v(7524.14, -1209) * mm});
            skLineSegment(sketch, "E305.left", {"start": v(7066.94, -751.8) * mm, "end": v(7066.94, -1209) * mm});
            skLineSegment(sketch, "E305.right", {"start": v(7524.14, -751.8) * mm, "end": v(7524.14, -1209) * mm});
            skLineSegment(sketch, "E306.bottom", {"start": v(7723.95, -751.8) * mm, "end": v(8181.15, -751.8) * mm});
            skLineSegment(sketch, "E306.top", {"start": v(7723.95, -1209) * mm, "end": v(8181.15, -1209) * mm});
            skLineSegment(sketch, "E306.left", {"start": v(7723.95, -751.8) * mm, "end": v(7723.95, -1209) * mm});
            skLineSegment(sketch, "E306.right", {"start": v(8181.15, -751.8) * mm, "end": v(8181.15, -1209) * mm});
            skSolve(sketch);
        }
        {
            var Q0;
            Q0 = qSketchRegion(id + "F62", true);
            extrude(context, id + "F63", {"entities" : qUnion([Q0]), "depth" : 1524 * mm});
        }
        {
            var Q0;
            Q0=makeQuery(id+"F1.opExtrude","CAP_FACE",FACE,{"disambiguationData":[OSD([sQuery(id+"F0.wireOp",EDGE,"E0.bottom"),sQuery(id+"F0.wireOp",EDGE,"E0.top"),sQuery(id+"F0.wireOp",EDGE,"E0.left"),sQuery(id+"F0.wireOp",EDGE,"E0.right")])],"isStart":true});
            var sketch = newSketch(context, id + "F64", { "sketchPlane" : qUnion([Q0])});
            skLineSegment(sketch, "E307.bottom", {"start": v(8105.67, -3848.25) * mm, "end": v(9934.47, -3848.25) * mm});
            skLineSegment(sketch, "E307.top", {"start": v(8105.67, -4610.25) * mm, "end": v(9934.47, -4610.25) * mm});
            skLineSegment(sketch, "E307.left", {"start": v(8105.67, -3848.25) * mm, "end": v(8105.67, -4610.25) * mm});
            skLineSegment(sketch, "E307.right", {"start": v(9934.47, -3848.25) * mm, "end": v(9934.47, -4610.25) * mm});
            skLineSegment(sketch, "E308.bottom", {"start": v(8105.67, -4622.95) * mm, "end": v(9934.47, -4622.95) * mm});
            skLineSegment(sketch, "E308.top", {"start": v(8105.67, -5384.95) * mm, "end": v(9934.47, -5384.95) * mm});
            skLineSegment(sketch, "E308.left", {"start": v(8105.67, -4622.95) * mm, "end": v(8105.67, -5384.95) * mm});
            skLineSegment(sketch, "E308.right", {"start": v(9934.47, -4622.95) * mm, "end": v(9934.47, -5384.95) * mm});
            skSolve(sketch);
        }
        {
            var Q0;
            Q0 = qSketchRegion(id + "F64", true);
            extrude(context, id + "F65", {"entities" : qUnion([Q0]), "depth" : 914.4 * mm});
        }
        {
            var Q0;
            Q0=makeQuery(id+"F1.opExtrude","CAP_FACE",FACE,{"disambiguationData":[OSD([sQuery(id+"F0.wireOp",EDGE,"E0.bottom"),sQuery(id+"F0.wireOp",EDGE,"E0.top"),sQuery(id+"F0.wireOp",EDGE,"E0.left"),sQuery(id+"F0.wireOp",EDGE,"E0.right")])],"isStart":true});
            var sketch = newSketch(context, id + "F66", { "sketchPlane" : qUnion([Q0])});
            skLineSegment(sketch, "E309.bottom", {"start": v(9945.95, -4622.85) * mm, "end": v(10707.95, -4622.85) * mm});
            skLineSegment(sketch, "E309.top", {"start": v(9945.95, -5384.85) * mm, "end": v(10707.95, -5384.85) * mm});
            skLineSegment(sketch, "E309.left", {"start": v(9945.95, -4622.85) * mm, "end": v(9945.95, -5384.85) * mm});
            skLineSegment(sketch, "E309.right", {"start": v(10707.95, -4622.85) * mm, "end": v(10707.95, -5384.85) * mm});
            skSolve(sketch);
        }
        {
            var Q0;
            Q0 = qSketchRegion(id + "F66", true);
            extrude(context, id + "F67", {"entities" : qUnion([Q0]), "depth" : 1130.3 * mm});
        }
    });
